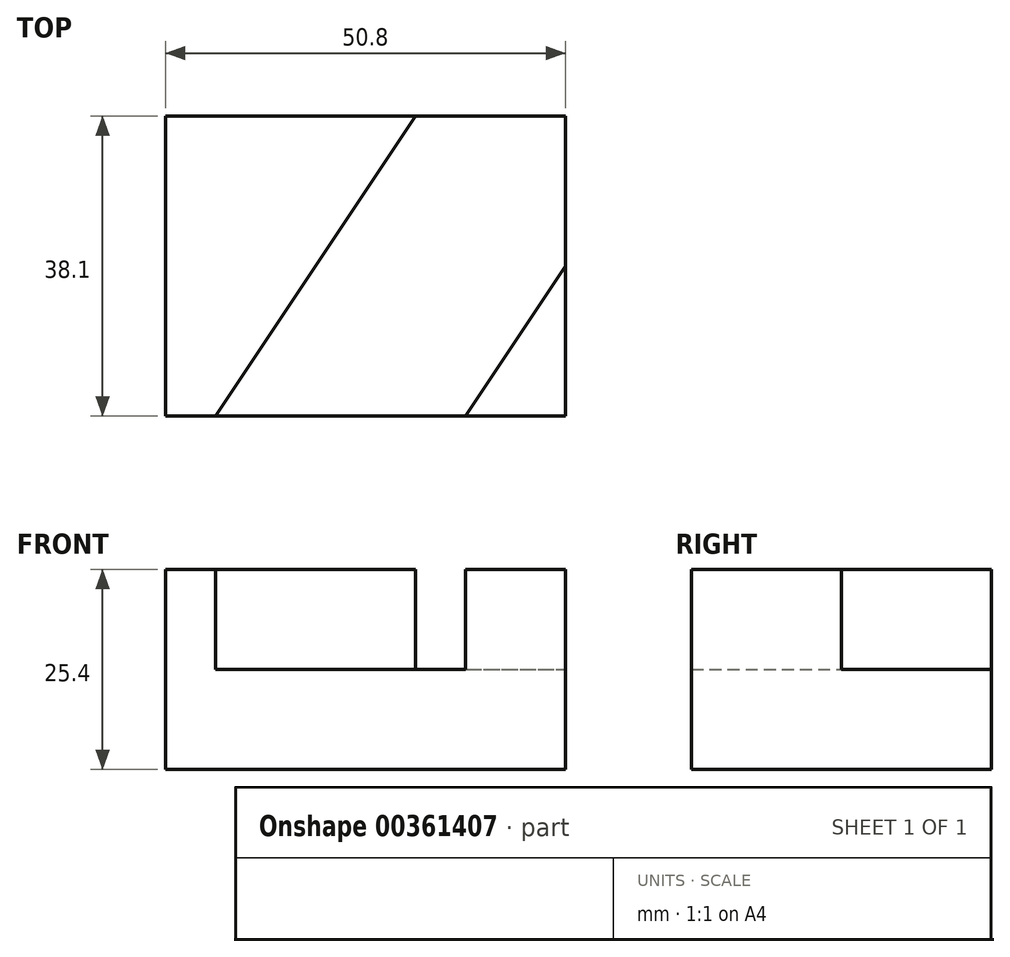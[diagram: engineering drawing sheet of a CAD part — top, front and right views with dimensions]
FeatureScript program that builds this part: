
annotation { "Feature Type Name" : "Feature", "Feature Type Description" : "" }
export const myFeature = defineFeature(function(context is Context, id is Id, definition is map)
    precondition{}
    {
        {
            var Q0;
            Q0=qCreatedBy(makeId("Front.planeOp"),FACE);
            var sketch = newSketch(context, id + "F0", { "sketchPlane" : qUnion([Q0])});
            skLineSegment(sketch, "E0", {"start": v(0, 0) * mm, "end": v(0, 25.4) * mm});
            skLineSegment(sketch, "E1", {"start": v(0, 25.4) * mm, "end": v(50.8, 25.4) * mm});
            skLineSegment(sketch, "E2", {"start": v(50.8, 25.4) * mm, "end": v(50.8, 0) * mm});
            skLineSegment(sketch, "E3", {"start": v(50.8, 0) * mm, "end": v(0, 0) * mm});
            skSolve(sketch);
        }
        {
            var Q0;
            Q0 = qSketchRegion(id + "F0", true);
            extrude(context, id + "F1", {"entities" : qUnion([Q0]), "oppositeDirection" : true, "depth" : 38.1 * mm});
        }
        {
            var Q0;
            Q0=makeQuery(id+"F1.opExtrude","SWEPT_FACE",FACE,{"disambiguationData":[OSD([sQuery(id+"F0.wireOp",EDGE,"E1")])]});
            var sketch = newSketch(context, id + "F2", { "sketchPlane" : qUnion([Q0])});
            skLineSegment(sketch, "E4", {"start": v(6.35, 0) * mm, "end": v(38.1, 0) * mm});
            skLineSegment(sketch, "E5", {"start": v(38.1, 0) * mm, "end": v(50.8, 19.05) * mm});
            skLineSegment(sketch, "E6", {"start": v(50.8, 19.05) * mm, "end": v(50.8, 38.1) * mm});
            skLineSegment(sketch, "E7", {"start": v(50.8, 38.1) * mm, "end": v(31.75, 38.1) * mm});
            skLineSegment(sketch, "E8", {"start": v(31.75, 38.1) * mm, "end": v(6.35, 0) * mm});
            skLineSegment(sketch, "E9", {"start": v(6.35, 0) * mm, "end": v(0, 0) * mm});
            skLineSegment(sketch, "E10", {"start": v(0, 0) * mm, "end": v(0, 38.1) * mm});
            skLineSegment(sketch, "E11", {"start": v(0, 38.1) * mm, "end": v(31.75, 38.1) * mm});
            skSolve(sketch);
        }
        {
            var Q0;
            Q0=makeQuery(id+"F2.imprint","IMPRINT",FACE,{"disambiguationData":[TD([[makeQuery(id+"F2.imprint","IMPRINT",EDGE,{"derivedFrom":sQuery(id+"F2.wireOp",EDGE,"E4")}),1.0]])]});
            extrude(context, id + "F3", {"entities" : qUnion([Q0]), "operationType" : NewBodyOperationType.REMOVE, "oppositeDirection" : true, "depth" : 12.7 * mm});
        }
    });
